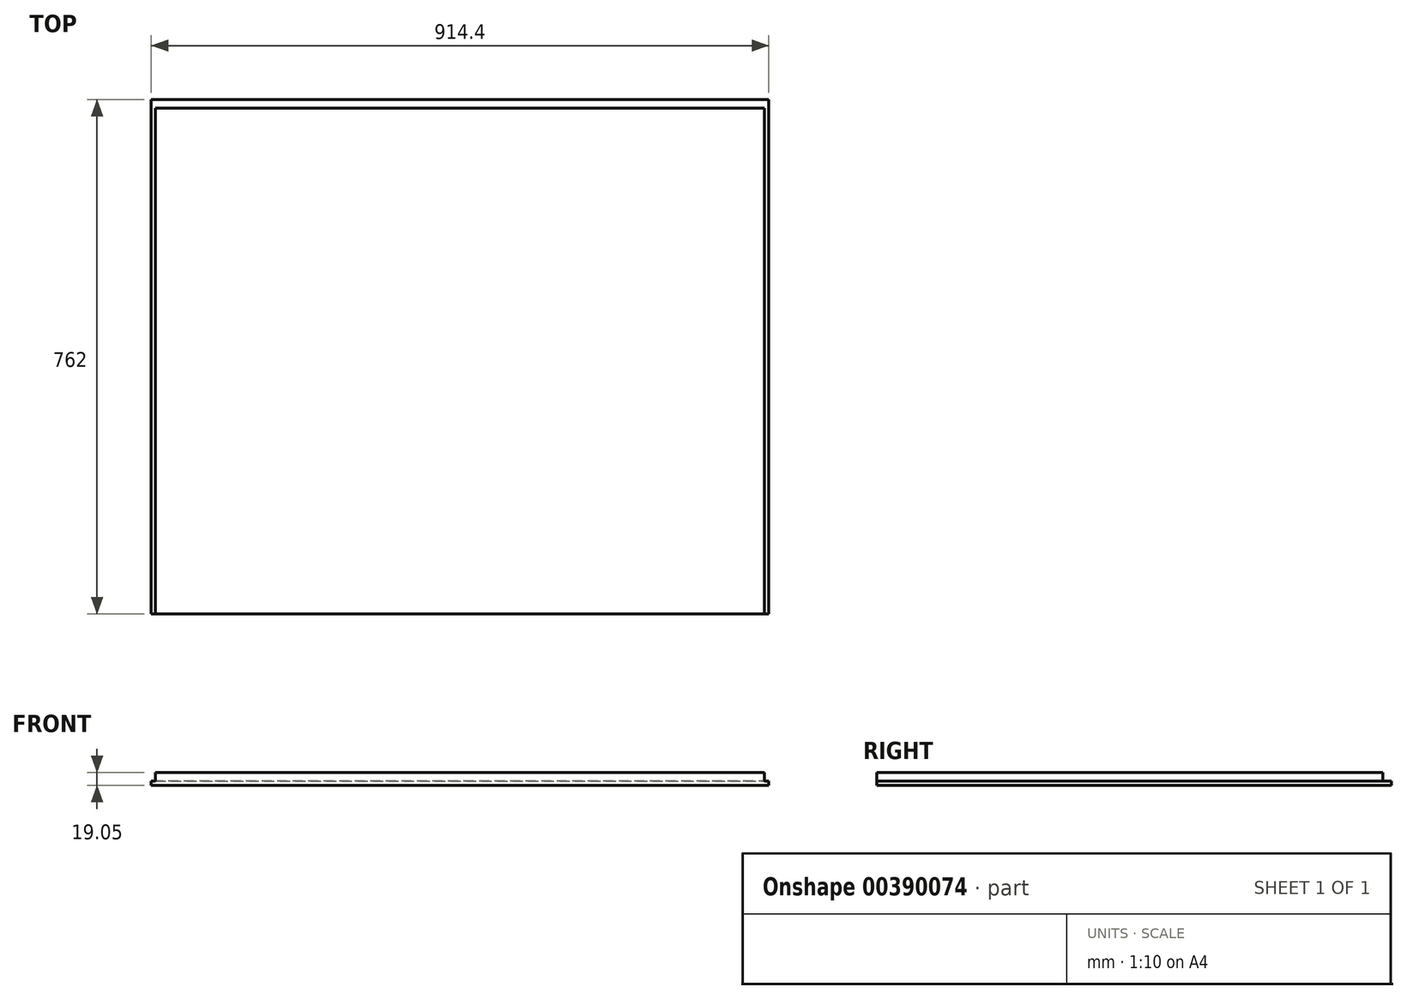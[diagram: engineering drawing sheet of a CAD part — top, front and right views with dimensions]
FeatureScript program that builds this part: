
annotation { "Feature Type Name" : "Feature", "Feature Type Description" : "" }
export const myFeature = defineFeature(function(context is Context, id is Id, definition is map)
    precondition{}
    {
        {
            var Q0;
            Q0=qCreatedBy(makeId("Top.planeOp"),FACE);
            var sketch = newSketch(context, id + "F0", { "sketchPlane" : qUnion([Q0])});
            skLineSegment(sketch, "E0.bottom", {"start": v(0, 0) * mm, "end": v(914.4, 0) * mm});
            skLineSegment(sketch, "E0.top", {"start": v(0, 762) * mm, "end": v(914.4, 762) * mm});
            skLineSegment(sketch, "E0.left", {"start": v(0, 0) * mm, "end": v(0, 762) * mm});
            skLineSegment(sketch, "E0.right", {"start": v(914.4, 0) * mm, "end": v(914.4, 762) * mm});
            skSolve(sketch);
        }
        {
            var Q0;
            Q0 = qSketchRegion(id + "F0", true);
            extrude(context, id + "F1", {"entities" : qUnion([Q0]), "depth" : 19.05 * mm});
        }
        {
            var Q0;
            Q0=makeQuery(id+"F1.opExtrude","SWEPT_FACE",FACE,{"disambiguationData":[OSD([sQuery(id+"F0.wireOp",EDGE,"E0.bottom")])]});
            var sketch = newSketch(context, id + "F2", { "sketchPlane" : qUnion([Q0])});
            skLineSegment(sketch, "E1", {"start": v(0, 19.05) * mm, "end": v(6.35, 19.05) * mm});
            skLineSegment(sketch, "E2", {"start": v(6.35, 19.05) * mm, "end": v(6.35, 6.35) * mm});
            skLineSegment(sketch, "E3", {"start": v(6.35, 6.35) * mm, "end": v(0, 6.35) * mm});
            skLineSegment(sketch, "E4", {"start": v(0, 6.35) * mm, "end": v(0, 19.05) * mm});
            skLineSegment(sketch, "E5", {"start": v(914.4, 19.05) * mm, "end": v(908.05, 19.05) * mm});
            skLineSegment(sketch, "E6", {"start": v(908.05, 19.05) * mm, "end": v(908.05, 6.35) * mm});
            skLineSegment(sketch, "E7", {"start": v(908.05, 6.35) * mm, "end": v(914.4, 6.35) * mm});
            skLineSegment(sketch, "E8", {"start": v(914.4, 6.35) * mm, "end": v(914.4, 19.05) * mm});
            skSolve(sketch);
        }
        {
            var Q0;
            Q0 = qSketchRegion(id + "F2", true);
            extrude(context, id + "F3", {"entities" : qUnion([Q0]), "operationType" : NewBodyOperationType.REMOVE, "endBound" : BoundingType.THROUGH_ALL, "oppositeDirection" : true, "depth" : 25.4 * mm});
        }
        {
            var Q0;
            Q0=makeQuery(id+"F1.opExtrude","SWEPT_FACE",FACE,{"disambiguationData":[OSD([sQuery(id+"F0.wireOp",EDGE,"E0.right")])]});
            var sketch = newSketch(context, id + "F4", { "sketchPlane" : qUnion([Q0])});
            skLineSegment(sketch, "E9", {"start": v(762, 6.35) * mm, "end": v(762, 19.05) * mm});
            skLineSegment(sketch, "E10", {"start": v(762, 19.05) * mm, "end": v(749.3, 19.05) * mm});
            skLineSegment(sketch, "E11", {"start": v(749.3, 19.05) * mm, "end": v(749.3, 6.35) * mm});
            skLineSegment(sketch, "E12", {"start": v(749.3, 6.35) * mm, "end": v(762, 6.35) * mm});
            skSolve(sketch);
        }
        {
            var Q0;
            Q0 = qSketchRegion(id + "F4", true);
            extrude(context, id + "F5", {"entities" : qUnion([Q0]), "operationType" : NewBodyOperationType.REMOVE, "endBound" : BoundingType.THROUGH_ALL, "oppositeDirection" : true, "depth" : 25.4 * mm});
        }
    });
